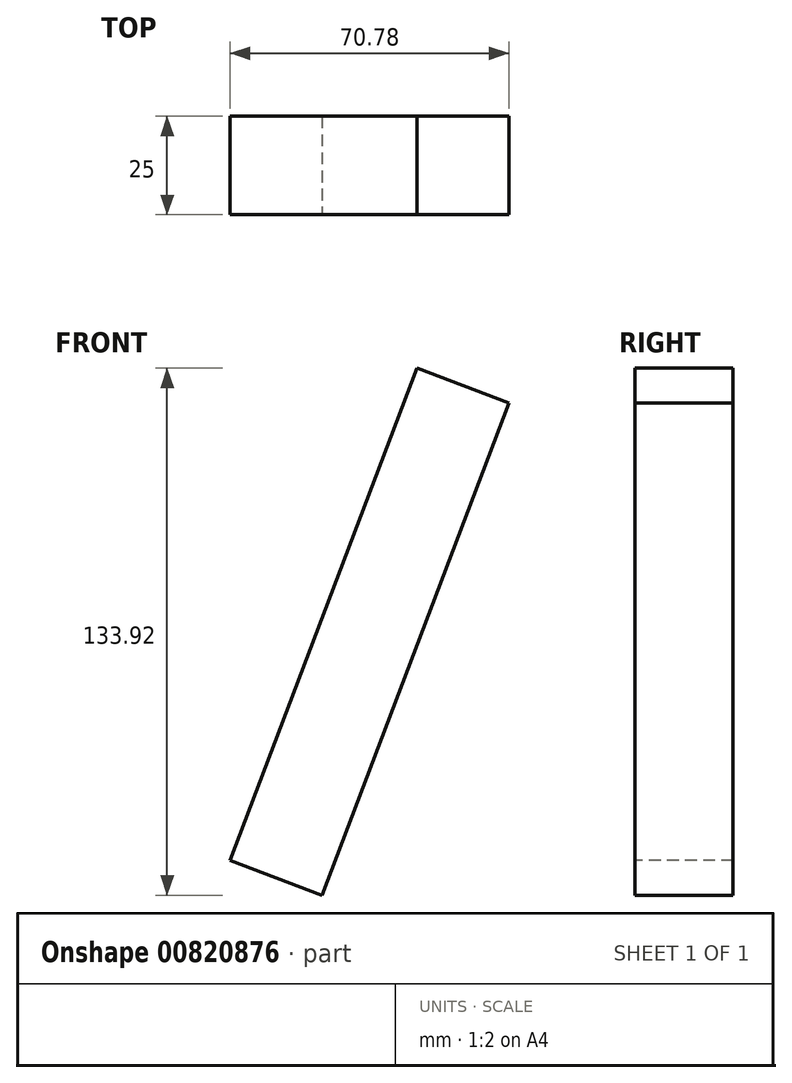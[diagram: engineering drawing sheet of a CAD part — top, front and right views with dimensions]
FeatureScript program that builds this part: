
annotation { "Feature Type Name" : "Feature", "Feature Type Description" : "" }
export const myFeature = defineFeature(function(context is Context, id is Id, definition is map)
    precondition{}
    {
        {
            var Q0;
            Q0=qCreatedBy(makeId("Front.planeOp"),FACE);
            var sketch = newSketch(context, id + "F0", { "sketchPlane" : qUnion([Q0])});
            skLineSegment(sketch, "E0", {"start": v(-115.55, -5.7) * mm, "end": v(-162.96, -130.76) * mm});
            skSolve(sketch);
        }
        {
            var Q0;
            Q0 = qSketchRegion(id + "F0", true);
            var Q1;
            Q1=sQuery(id+"F0.wireOp",EDGE,"E0");
            extrude(context, id + "F1", {"entities" : qUnion([Q0]), "bodyType" : ToolBodyType.SURFACE, "surfaceEntities" : qUnion([Q1]), "depth" : 25 * mm, "offsetDistance" : 25 * mm});
        }
        {
            var Q0;
            Q0=makeQuery(id+"F1.opExtrude","SWEPT_FACE",FACE,{"disambiguationData":[OSD([sQuery(id+"F0.wireOp",EDGE,"E0")])]});
            extrude(context, id + "F2", {"entities" : qUnion([Q0]), "depth" : 25 * mm, "offsetDistance" : 25 * mm});
        }
    });
